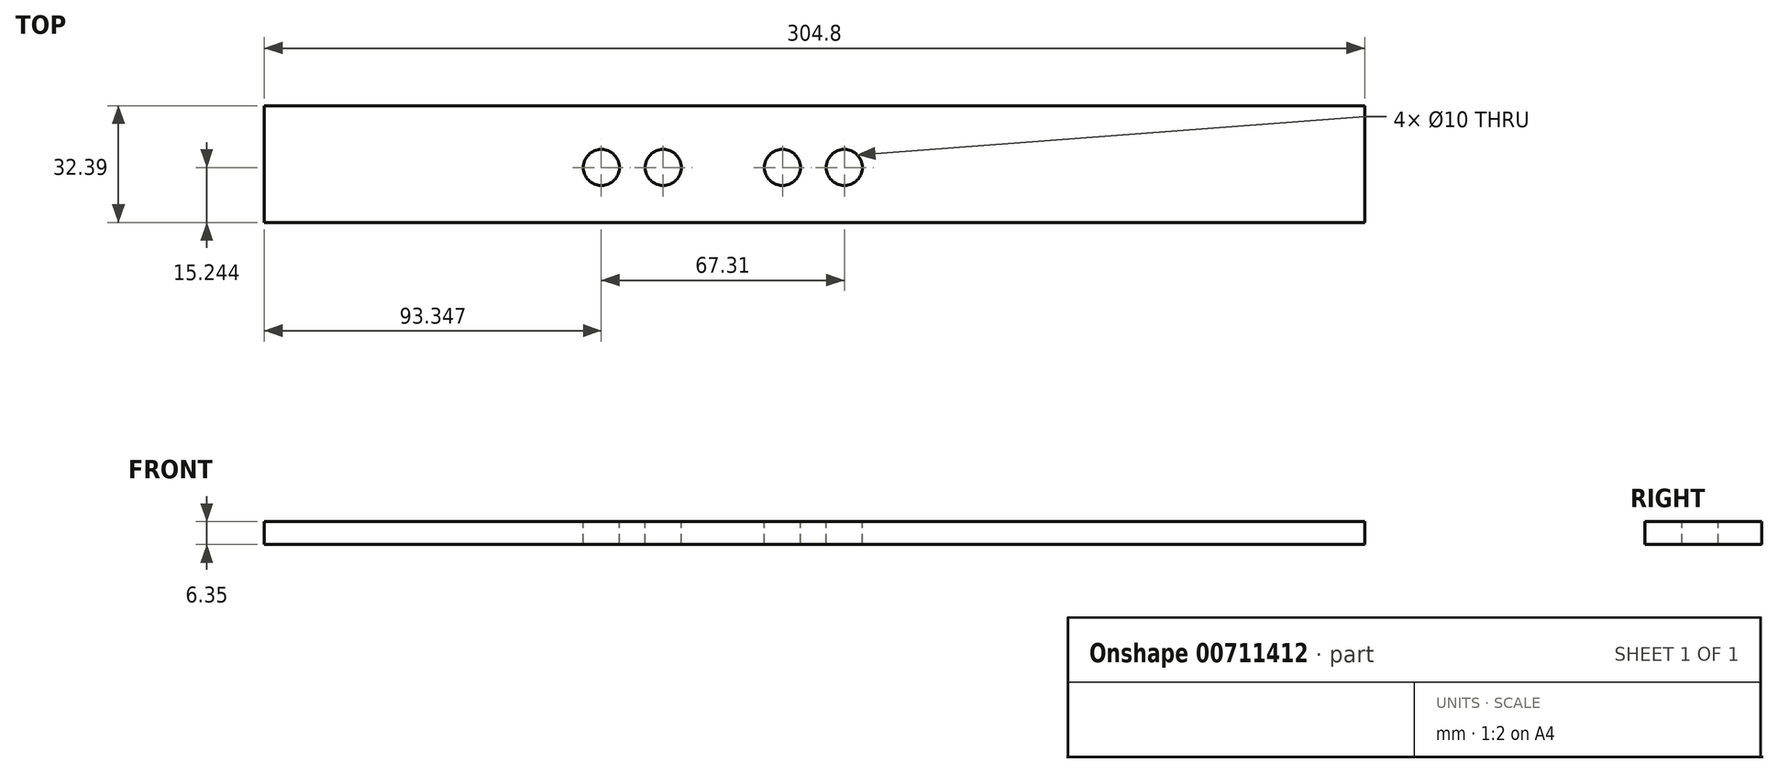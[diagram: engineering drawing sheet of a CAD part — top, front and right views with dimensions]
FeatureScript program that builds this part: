
annotation { "Feature Type Name" : "Feature", "Feature Type Description" : "" }
export const myFeature = defineFeature(function(context is Context, id is Id, definition is map)
    precondition{}
    {
        {
            var Q0;
            Q0=qCreatedBy(makeId("Top.planeOp"),FACE);
            var sketch = newSketch(context, id + "F0", { "sketchPlane" : qUnion([Q0])});
            skLineSegment(sketch, "E0.top", {"start": v(-51.98, 15.9) * mm, "end": v(49.62, 15.9) * mm});
            skLineSegment(sketch, "E1", {"start": v(-51.98, -1.24) * mm, "end": v(49.62, -1.24) * mm});
            skLineSegment(sketch, "E2", {"start": v(-34.83, 15.9) * mm, "end": v(-34.83, -1.24) * mm});
            skLineSegment(sketch, "E3", {"start": v(-17.69, 15.9) * mm, "end": v(-17.69, -1.24) * mm});
            skLineSegment(sketch, "E4", {"start": v(15.33, 15.9) * mm, "end": v(15.33, -1.24) * mm});
            skLineSegment(sketch, "E5", {"start": v(32.48, 15.9) * mm, "end": v(32.48, -1.24) * mm});
            skCircle(sketch, "E6", {"center": v(-34.83, -1.24) * mm, "radius": 5 * mm});
            skCircle(sketch, "E7", {"center": v(-17.69, -1.24) * mm, "radius": 5 * mm});
            skCircle(sketch, "E8", {"center": v(15.33, -1.24) * mm, "radius": 5 * mm});
            skCircle(sketch, "E9", {"center": v(32.48, -1.24) * mm, "radius": 5 * mm});
            skLineSegment(sketch, "E10", {"start": v(-51.98, 15.9) * mm, "end": v(-51.98, -1.24) * mm});
            skLineSegment(sketch, "E11", {"start": v(49.62, 15.9) * mm, "end": v(49.62, -1.24) * mm});
            skLineSegment(sketch, "E12.bottom", {"start": v(-51.98, 15.9) * mm, "end": v(-128.18, 15.9) * mm});
            skLineSegment(sketch, "E12.top", {"start": v(-51.98, -1.24) * mm, "end": v(-128.18, -1.24) * mm});
            skLineSegment(sketch, "E12.right", {"start": v(-128.18, 15.9) * mm, "end": v(-128.18, -1.24) * mm});
            skLineSegment(sketch, "E13.bottom", {"start": v(-128.18, -1.24) * mm, "end": v(-51.98, -1.24) * mm});
            skLineSegment(sketch, "E13.top", {"start": v(-128.18, -16.48) * mm, "end": v(-51.98, -16.48) * mm});
            skLineSegment(sketch, "E13.left", {"start": v(-128.18, -1.24) * mm, "end": v(-128.18, -16.48) * mm});
            skLineSegment(sketch, "E13.right", {"start": v(-51.98, -1.24) * mm, "end": v(-51.98, -16.48) * mm});
            skLineSegment(sketch, "E14.bottom", {"start": v(-51.98, -16.48) * mm, "end": v(49.62, -16.48) * mm});
            skLineSegment(sketch, "E14.left", {"start": v(-51.98, -16.48) * mm, "end": v(-51.98, -1.24) * mm});
            skLineSegment(sketch, "E14.right", {"start": v(49.62, -16.48) * mm, "end": v(49.62, -1.24) * mm});
            skLineSegment(sketch, "E15.bottom", {"start": v(49.62, 15.9) * mm, "end": v(176.62, 15.9) * mm});
            skLineSegment(sketch, "E15.top", {"start": v(49.62, -16.48) * mm, "end": v(176.62, -16.48) * mm});
            skLineSegment(sketch, "E15.left", {"start": v(49.62, 15.9) * mm, "end": v(49.62, -16.48) * mm});
            skLineSegment(sketch, "E15.right", {"start": v(176.62, 15.9) * mm, "end": v(176.62, -16.48) * mm});
            skSolve(sketch);
        }
        {
            var Q0;
            Q0 = qSketchRegion(id + "F0", true);
            extrude(context, id + "F1", {"entities" : qUnion([Q0]), "depth" : -6.35 * mm, "offsetDistance" : 25.4 * mm});
        }
    });
